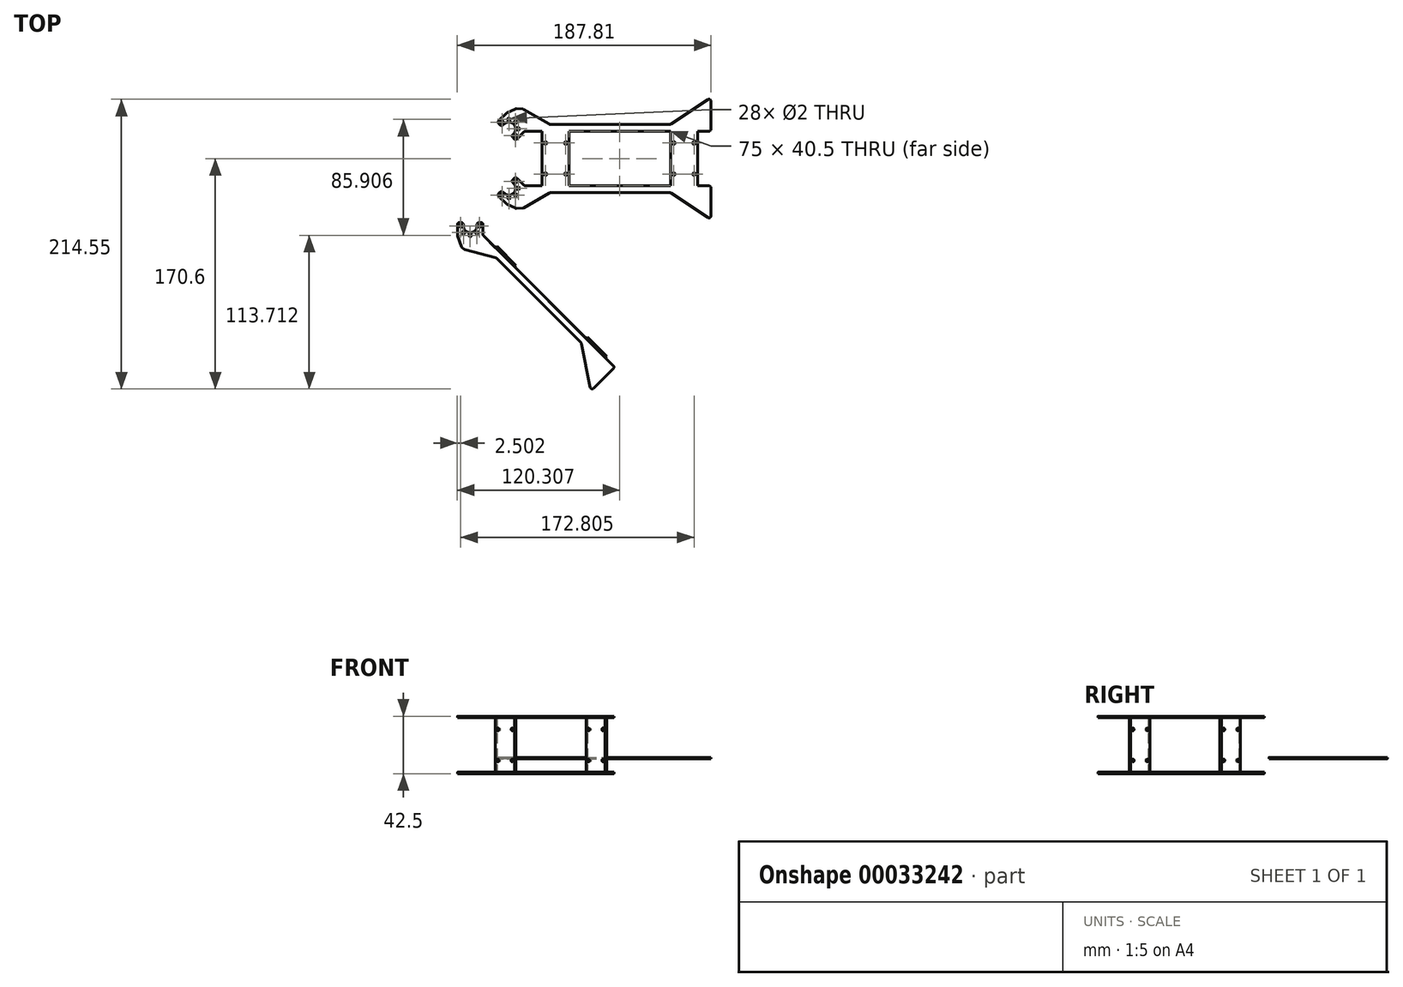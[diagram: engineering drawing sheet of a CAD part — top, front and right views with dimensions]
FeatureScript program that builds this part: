
annotation { "Feature Type Name" : "Feature", "Feature Type Description" : "" }
export const myFeature = defineFeature(function(context is Context, id is Id, definition is map)
    precondition{}
    {
        {
            var Q0;
            Q0=qCreatedBy(makeId("Top.planeOp"),FACE);
            var sketch = newSketch(context, id + "F0", { "sketchPlane" : qUnion([Q0])});
            skArc(sketch, "E0", {"start": v(-5.05, 0) * mm, "mid": v(0, -5.05) * mm, "end": v(5.05, 0) * mm});
            skCircle(sketch, "E1", {"center": v(-7, 0) * mm, "radius": 1 * mm});
            skCircle(sketch, "E2.1.0", {"center": v(-4.95, -4.95) * mm, "radius": 1 * mm});
            skCircle(sketch, "E2.2.0", {"center": v(0, -7) * mm, "radius": 1 * mm});
            skCircle(sketch, "E2.3.0", {"center": v(4.95, -4.95) * mm, "radius": 1 * mm});
            skCircle(sketch, "E2.4.0", {"center": v(7, 0) * mm, "radius": 1 * mm});
            skLineSegment(sketch, "E3", {"start": v(0, 0) * mm, "end": v(106.07, -106.07) * mm, "construction": true});
            skLineSegment(sketch, "E4", {"start": v(9.5, 0) * mm, "end": v(9.5, -7) * mm});
            skLineSegment(sketch, "E5", {"start": v(9.5, -7) * mm, "end": v(107.08, -104.58) * mm});
            skLineSegment(sketch, "E6.MirrorCS", {"start": v(-9.5, 0) * mm, "end": v(-9.5, -7) * mm});
            skLineSegment(sketch, "E7", {"start": v(-9.5, -7) * mm, "end": v(-5.85, -17.02) * mm});
            skLineSegment(sketch, "E8", {"start": v(-5.85, -17.02) * mm, "end": v(19.15, -23.72) * mm});
            skLineSegment(sketch, "E9", {"start": v(19.15, -23.72) * mm, "end": v(103.55, -108.12) * mm});
            skLineSegment(sketch, "E10", {"start": v(107.08, -104.58) * mm, "end": v(103.55, -108.12) * mm});
            skLineSegment(sketch, "E11", {"start": v(-9.5, 0) * mm, "end": v(-9.5, 2.5) * mm});
            skLineSegment(sketch, "E12", {"start": v(-9.5, 2.5) * mm, "end": v(-5.05, 2.5) * mm});
            skLineSegment(sketch, "E13", {"start": v(9.5, 2.5) * mm, "end": v(9.5, 0) * mm});
            skLineSegment(sketch, "E14", {"start": v(-5.05, 0) * mm, "end": v(-5.05, 2.5) * mm});
            skLineSegment(sketch, "E15.MirrorCS", {"start": v(5.05, 0) * mm, "end": v(5.05, 2.5) * mm});
            skLineSegment(sketch, "E16.trimOffspring", {"start": v(5.05, 2.5) * mm, "end": v(9.5, 2.5) * mm});
            skLineSegment(sketch, "E17", {"start": v(103.55, -108.12) * mm, "end": v(89.4, -122.26) * mm});
            skLineSegment(sketch, "E18", {"start": v(89.4, -122.26) * mm, "end": v(82.33, -86.9) * mm});
            skSolve(sketch);
        }
        {
            var Q0;
            Q0=qSketchRegion(id+"F0",true);
            extrude(context, id + "F1", {"entities" : qUnion([Q0]), "depth" : 1 * mm});
        }
        {
            var Q0;
            Q0=makeQuery(id+"F1.opExtrude","SWEPT_EDGE",EDGE,{"disambiguationData":[OSD([sQuery(id+"F0.wireOp",EDGE,"E17"),sQuery(id+"F0.wireOp",EDGE,"E18")])]});
            var Q1;
            Q1=makeQuery(id+"F1.opExtrude","SWEPT_EDGE",EDGE,{"disambiguationData":[OSD([sQuery(id+"F0.wireOp",EDGE,"E9"),sQuery(id+"F0.wireOp",EDGE,"E18")])]});
            var Q2;
            Q2=makeQuery(id+"F1.opExtrude","SWEPT_EDGE",EDGE,{"disambiguationData":[OSD([sQuery(id+"F0.wireOp",EDGE,"E5"),sQuery(id+"F0.wireOp",EDGE,"E10")])]});
            var Q3;
            Q3=makeQuery(id+"F1.opExtrude","SWEPT_EDGE",EDGE,{"disambiguationData":[OSD([sQuery(id+"F0.wireOp",EDGE,"E8"),sQuery(id+"F0.wireOp",EDGE,"E9")])]});
            var Q4;
            Q4=makeQuery(id+"F1.opExtrude","SWEPT_EDGE",EDGE,{"disambiguationData":[OSD([sQuery(id+"F0.wireOp",EDGE,"E4"),sQuery(id+"F0.wireOp",EDGE,"E5")])]});
            var Q5;
            Q5=makeQuery(id+"F1.opExtrude","SWEPT_EDGE",EDGE,{"disambiguationData":[OSD([sQuery(id+"F0.wireOp",EDGE,"E13"),sQuery(id+"F0.wireOp",EDGE,"E16.trimOffspring")])]});
            var Q6;
            Q6=makeQuery(id+"F1.opExtrude","SWEPT_EDGE",EDGE,{"disambiguationData":[OSD([sQuery(id+"F0.wireOp",EDGE,"E12"),sQuery(id+"F0.wireOp",EDGE,"E14")])]});
            var Q7;
            Q7=makeQuery(id+"F1.opExtrude","SWEPT_EDGE",EDGE,{"disambiguationData":[OSD([sQuery(id+"F0.wireOp",EDGE,"E15.MirrorCS"),sQuery(id+"F0.wireOp",EDGE,"E16.trimOffspring")])]});
            var Q8;
            Q8=makeQuery(id+"F1.opExtrude","SWEPT_EDGE",EDGE,{"disambiguationData":[OSD([sQuery(id+"F0.wireOp",EDGE,"E11"),sQuery(id+"F0.wireOp",EDGE,"E12")])]});
            var Q9;
            Q9=makeQuery(id+"F1.opExtrude","SWEPT_EDGE",EDGE,{"disambiguationData":[OSD([sQuery(id+"F0.wireOp",EDGE,"E6.MirrorCS"),sQuery(id+"F0.wireOp",EDGE,"E7")])]});
            fillet(context, id + "F2", {"entities" : qUnion([Q0, Q1, Q2, Q3, Q4, Q5, Q6, Q7, Q8, Q9]), "radius" : 1.5 * mm, "tangentPropagation" : true, "allowEdgeOverflow" : false});
        }
        {
            var Q0;
            Q0=makeQuery(id+"F1.opExtrude","SWEPT_EDGE",EDGE,{"disambiguationData":[OSD([sQuery(id+"F0.wireOp",EDGE,"E7"),sQuery(id+"F0.wireOp",EDGE,"E8")])]});
            chamfer(context, id + "F3", {"entities" : qUnion([Q0]), "width" : 3 * mm, "tangentPropagation" : true});
        }
        {
            var Q0;
            {var subQ0=sQuery(id+"F0.wireOp",EDGE,"E7");Q0=makeQuery(id+"F3.opChamfer","BLEND_EDGE",EDGE,{"blendedFrom":[makeQuery(id+"F1.opExtrude","SWEPT_EDGE",EDGE,{"disambiguationData":[OSD([subQ0,sQuery(id+"F0.wireOp",EDGE,"E8")])]}),makeQuery(id+"F1.opExtrude","SWEPT_FACE",FACE,{"disambiguationData":[OSD([subQ0])]})],"blendedInto":[makeQuery(id+"F1.opExtrude","SWEPT_FACE",FACE,{"disambiguationData":[OSD([subQ0])]})]});}
            var Q1;
            {var subQ0=sQuery(id+"F0.wireOp",EDGE,"E8");Q1=makeQuery(id+"F3.opChamfer","BLEND_EDGE",EDGE,{"blendedFrom":[makeQuery(id+"F1.opExtrude","SWEPT_EDGE",EDGE,{"disambiguationData":[OSD([sQuery(id+"F0.wireOp",EDGE,"E7"),subQ0])]}),makeQuery(id+"F1.opExtrude","SWEPT_FACE",FACE,{"disambiguationData":[OSD([subQ0])]})],"blendedInto":[makeQuery(id+"F1.opExtrude","SWEPT_FACE",FACE,{"disambiguationData":[OSD([subQ0])]})]});}
            fillet(context, id + "F4", {"entities" : qUnion([Q0, Q1]), "radius" : 1.5 * mm, "tangentPropagation" : true, "allowEdgeOverflow" : false});
        }
        {
            var Q0;
            Q0=makeQuery(id+"F1.opExtrude","CAP_FACE",FACE,{"disambiguationData":[OSD([sQuery(id+"F0.wireOp",EDGE,"E0"),sQuery(id+"F0.wireOp",EDGE,"E1"),sQuery(id+"F0.wireOp",EDGE,"E2.1.0"),sQuery(id+"F0.wireOp",EDGE,"E2.2.0"),sQuery(id+"F0.wireOp",EDGE,"E2.3.0"),sQuery(id+"F0.wireOp",EDGE,"E2.4.0"),sQuery(id+"F0.wireOp",EDGE,"E4"),sQuery(id+"F0.wireOp",EDGE,"E5"),sQuery(id+"F0.wireOp",EDGE,"E6.MirrorCS"),sQuery(id+"F0.wireOp",EDGE,"E7"),sQuery(id+"F0.wireOp",EDGE,"E8"),sQuery(id+"F0.wireOp",EDGE,"E9"),sQuery(id+"F0.wireOp",EDGE,"E10"),sQuery(id+"F0.wireOp",EDGE,"E11"),sQuery(id+"F0.wireOp",EDGE,"E12"),sQuery(id+"F0.wireOp",EDGE,"E13"),sQuery(id+"F0.wireOp",EDGE,"E14"),sQuery(id+"F0.wireOp",EDGE,"E15.MirrorCS"),sQuery(id+"F0.wireOp",EDGE,"E16.trimOffspring"),sQuery(id+"F0.wireOp",EDGE,"E17"),sQuery(id+"F0.wireOp",EDGE,"E18")])],"isStart":false});
            var sketch = newSketch(context, id + "F5", { "sketchPlane" : qUnion([Q0])});
            skLineSegment(sketch, "E19", {"start": v(18.7, -16.2) * mm, "end": v(19.75, -15.13) * mm});
            skLineSegment(sketch, "E20", {"start": v(19.75, -15.13) * mm, "end": v(33.9, -29.27) * mm});
            skLineSegment(sketch, "E21", {"start": v(33.9, -29.27) * mm, "end": v(32.83, -30.33) * mm});
            skLineSegment(sketch, "E22", {"start": v(18.7, -16.2) * mm, "end": v(32.83, -30.33) * mm});
            skLineSegment(sketch, "E23", {"start": v(100, -97.5) * mm, "end": v(85.87, -83.37) * mm});
            skLineSegment(sketch, "E24", {"start": v(85.87, -83.37) * mm, "end": v(86.93, -82.3) * mm});
            skLineSegment(sketch, "E25", {"start": v(86.93, -82.3) * mm, "end": v(101.07, -96.45) * mm});
            skLineSegment(sketch, "E26", {"start": v(101.07, -96.45) * mm, "end": v(100, -97.5) * mm});
            skSolve(sketch);
        }
        {
            var Q0;
            Q0=qSketchRegion(id+"F5",true);
            extrude(context, id + "F6", {"entities" : qUnion([Q0]), "operationType" : NewBodyOperationType.ADD, "depth" : (40.5 / 2) * mm, "hasSecondDirection" : true, "secondDirectionOppositeDirection" : true, "secondDirectionDepth" : 1 * mm});
        }
        {
            var Q0;
            Q0=makeQuery(id+"F6.opExtrude","CAP_FACE",FACE,{"disambiguationData":[OSD([sQuery(id+"F5.wireOp",EDGE,"E19"),sQuery(id+"F5.wireOp",EDGE,"E20"),sQuery(id+"F5.wireOp",EDGE,"E21"),sQuery(id+"F5.wireOp",EDGE,"E22")])],"isStart":false});
            cPlane(context, id + "F7", {"entities" : qUnion([Q0]), "cplaneType" : CPlaneType.OFFSET, "offset" : 0 * mm, "width" : 150 * mm, "height" : 150 * mm});
        }
        {
            var Q0;
            Q0=makeQuery(id+"F1.opExtrude","SWEPT_BODY",BODY,{"disambiguationData":[OSD([sQuery(id+"F0.wireOp",EDGE,"E0"),sQuery(id+"F0.wireOp",EDGE,"E1"),sQuery(id+"F0.wireOp",EDGE,"E2.1.0"),sQuery(id+"F0.wireOp",EDGE,"E2.2.0"),sQuery(id+"F0.wireOp",EDGE,"E2.3.0"),sQuery(id+"F0.wireOp",EDGE,"E2.4.0"),sQuery(id+"F0.wireOp",EDGE,"E4"),sQuery(id+"F0.wireOp",EDGE,"E5"),sQuery(id+"F0.wireOp",EDGE,"E6.MirrorCS"),sQuery(id+"F0.wireOp",EDGE,"E7"),sQuery(id+"F0.wireOp",EDGE,"E8"),sQuery(id+"F0.wireOp",EDGE,"E9"),sQuery(id+"F0.wireOp",EDGE,"E10"),sQuery(id+"F0.wireOp",EDGE,"E11"),sQuery(id+"F0.wireOp",EDGE,"E12"),sQuery(id+"F0.wireOp",EDGE,"E13"),sQuery(id+"F0.wireOp",EDGE,"E14"),sQuery(id+"F0.wireOp",EDGE,"E15.MirrorCS"),sQuery(id+"F0.wireOp",EDGE,"E16.trimOffspring"),sQuery(id+"F0.wireOp",EDGE,"E17"),sQuery(id+"F0.wireOp",EDGE,"E18")])]});
            var Q1;
            Q1=qCreatedBy(id+"F7.planeOp",FACE);
            mirror(context, id + "F8", {"operationType" : NewBodyOperationType.ADD, "entities" : qUnion([Q0]), "mirrorPlane" : qUnion([Q1])});
        }
        {
            var Q0;
            {var subQ0=makeQuery(id+"F6.opExtrude","SWEPT_FACE",FACE,{"disambiguationData":[OSD([sQuery(id+"F5.wireOp",EDGE,"E20")])]});Q0=makeQuery(id+"F8.boolean.opBoolean","MERGE",FACE,{"derivedFrom":[subQ0,makeQuery(id+"F8.opPattern","COPY",FACE,{"derivedFrom":subQ0,"instanceName":"1"})]});}
            var sketch = newSketch(context, id + "F9", { "sketchPlane" : qUnion([Q0])});
            skLineSegment(sketch, "E27", {"start": v(-24.67, 21.25) * mm, "end": v(-44.67, 21.25) * mm, "construction": true});
            skLineSegment(sketch, "E28.bottom", {"start": v(-27.17, 32.75) * mm, "end": v(-42.17, 32.75) * mm, "construction": true});
            skLineSegment(sketch, "E28.top", {"start": v(-27.17, 9.75) * mm, "end": v(-42.17, 9.75) * mm, "construction": true});
            skLineSegment(sketch, "E28.left", {"start": v(-27.17, 32.75) * mm, "end": v(-27.17, 9.75) * mm, "construction": true});
            skLineSegment(sketch, "E28.right", {"start": v(-42.17, 32.75) * mm, "end": v(-42.17, 9.75) * mm, "construction": true});
            skPoint(sketch, "E28.middle", {"position": v(-34.67, 21.25) * mm});
            skCircle(sketch, "E29", {"center": v(-27.17, 32.75) * mm, "radius": 1 * mm});
            skLineSegment(sketch, "E30", {"start": v(-34.67, 32.75) * mm, "end": v(-34.67, 9.75) * mm, "construction": true});
            skCircle(sketch, "E31.MirrorC", {"center": v(-27.17, 9.75) * mm, "radius": 1 * mm});
            skCircle(sketch, "E32.MirrorC", {"center": v(-42.17, 32.75) * mm, "radius": 1 * mm});
            skCircle(sketch, "E33.MirrorC", {"center": v(-42.17, 9.75) * mm, "radius": 1 * mm});
            skLineSegment(sketch, "E34.1.0.0", {"start": v(-122.17, 32.75) * mm, "end": v(-137.17, 32.75) * mm, "construction": true});
            skLineSegment(sketch, "E34.1.0.1", {"start": v(-129.67, 32.75) * mm, "end": v(-129.67, 9.75) * mm, "construction": true});
            skLineSegment(sketch, "E34.1.0.2", {"start": v(-122.17, 32.75) * mm, "end": v(-122.17, 9.75) * mm, "construction": true});
            skLineSegment(sketch, "E34.1.0.3", {"start": v(-119.67, 21.25) * mm, "end": v(-139.67, 21.25) * mm, "construction": true});
            skLineSegment(sketch, "E34.1.0.4", {"start": v(-137.17, 32.75) * mm, "end": v(-137.17, 9.75) * mm, "construction": true});
            skLineSegment(sketch, "E34.1.0.5", {"start": v(-122.17, 9.75) * mm, "end": v(-137.17, 9.75) * mm, "construction": true});
            skPoint(sketch, "E34.1.0.6", {"position": v(-129.67, 21.25) * mm});
            skCircle(sketch, "E34.1.0.7", {"center": v(-137.17, 32.75) * mm, "radius": 1 * mm});
            skCircle(sketch, "E34.1.0.8", {"center": v(-137.17, 9.75) * mm, "radius": 1 * mm});
            skCircle(sketch, "E34.1.0.9", {"center": v(-122.17, 9.75) * mm, "radius": 1 * mm});
            skCircle(sketch, "E34.1.0.10", {"center": v(-122.17, 32.75) * mm, "radius": 1 * mm});
            skLineSegment(sketch, "E34.direction1", {"start": v(-42.17, 9.75) * mm, "end": v(-137.17, 9.75) * mm, "construction": true});
            skSolve(sketch);
        }
        {
            var Q0;
            Q0=qSketchRegion(id+"F9",true);
            extrude(context, id + "F10", {"entities" : qUnion([Q0]), "operationType" : NewBodyOperationType.REMOVE, "endBound" : BoundingType.UP_TO_NEXT, "oppositeDirection" : true, "depth" : 25 * mm});
        }
        {
            var Q0;
            {var subQ0=makeQuery(id+"F6.opExtrude","SWEPT_FACE",FACE,{"disambiguationData":[OSD([sQuery(id+"F5.wireOp",EDGE,"E26")])]});Q0=makeQuery(id+"F8.boolean.opBoolean","MERGE",FACE,{"derivedFrom":[subQ0,makeQuery(id+"F8.opPattern","COPY",FACE,{"derivedFrom":subQ0,"instanceName":"1"})]});}
            var sketch = newSketch(context, id + "F11", { "sketchPlane" : qUnion([Q0])});
            skLineSegment(sketch, "E35.bottom", {"start": v(1.77, 42.5) * mm, "end": v(3.27, 42.5) * mm});
            skLineSegment(sketch, "E35.top", {"start": v(1.77, 41.5) * mm, "end": v(3.27, 41.5) * mm});
            skLineSegment(sketch, "E35.left", {"start": v(1.77, 42.5) * mm, "end": v(1.77, 41.5) * mm});
            skLineSegment(sketch, "E35.right", {"start": v(3.27, 42.5) * mm, "end": v(3.27, 41.5) * mm});
            skLineSegment(sketch, "E36.bottom", {"start": v(1.77, 0) * mm, "end": v(3.27, 0) * mm});
            skLineSegment(sketch, "E36.top", {"start": v(1.77, 1) * mm, "end": v(3.27, 1) * mm});
            skLineSegment(sketch, "E36.left", {"start": v(1.77, 0) * mm, "end": v(1.77, 1) * mm});
            skLineSegment(sketch, "E36.right", {"start": v(3.27, 0) * mm, "end": v(3.27, 1) * mm});
            skSolve(sketch);
        }
        {
            var Q0;
            Q0 = qSketchRegion(id + "F11", true);
            var Q1;
            {var subQ0=makeQuery(id+"F6.opExtrude","SWEPT_FACE",FACE,{"disambiguationData":[OSD([sQuery(id+"F5.wireOp",EDGE,"E19")])]});Q1=makeQuery(id+"F8.boolean.opBoolean","MERGE",FACE,{"derivedFrom":[subQ0,makeQuery(id+"F8.opPattern","COPY",FACE,{"derivedFrom":subQ0,"instanceName":"1"})]});}
            extrude(context, id + "F12", {"entities" : qUnion([Q0]), "operationType" : NewBodyOperationType.REMOVE, "endBound" : BoundingType.UP_TO_SURFACE, "oppositeDirection" : true, "endBoundEntityFace" : qUnion([Q1]), "depth" : 25 * mm});
        }
        {
            var Q0;
            Q0=makeQuery(id+"F12.boolean.opBoolean","SPLIT",BODY,{"disambiguationData":[OD(0.0)],"derivedFrom":makeQuery(id+"F1.opExtrude","SWEPT_BODY",BODY,{"disambiguationData":[OSD([sQuery(id+"F0.wireOp",EDGE,"E0"),sQuery(id+"F0.wireOp",EDGE,"E1"),sQuery(id+"F0.wireOp",EDGE,"E2.1.0"),sQuery(id+"F0.wireOp",EDGE,"E2.2.0"),sQuery(id+"F0.wireOp",EDGE,"E2.3.0"),sQuery(id+"F0.wireOp",EDGE,"E2.4.0"),sQuery(id+"F0.wireOp",EDGE,"E4"),sQuery(id+"F0.wireOp",EDGE,"E5"),sQuery(id+"F0.wireOp",EDGE,"E6.MirrorCS"),sQuery(id+"F0.wireOp",EDGE,"E7"),sQuery(id+"F0.wireOp",EDGE,"E8"),sQuery(id+"F0.wireOp",EDGE,"E9"),sQuery(id+"F0.wireOp",EDGE,"E10"),sQuery(id+"F0.wireOp",EDGE,"E11"),sQuery(id+"F0.wireOp",EDGE,"E12"),sQuery(id+"F0.wireOp",EDGE,"E13"),sQuery(id+"F0.wireOp",EDGE,"E14"),sQuery(id+"F0.wireOp",EDGE,"E15.MirrorCS"),sQuery(id+"F0.wireOp",EDGE,"E16.trimOffspring"),sQuery(id+"F0.wireOp",EDGE,"E17"),sQuery(id+"F0.wireOp",EDGE,"E18")])]})});
            var Q1;
            {var subQ0=sQuery(id+"F5.wireOp",EDGE,"E26");var subQ1=sQuery(id+"F5.wireOp",EDGE,"E23");var subQ2=sQuery(id+"F0.wireOp",EDGE,"E5");var subQ3=makeQuery(id+"F6.opExtrude","SWEPT_FACE",FACE,{"disambiguationData":[OSD([sQuery(id+"F5.wireOp",EDGE,"E22")])]});var subQ4=makeQuery(id+"F6.opExtrude","SWEPT_FACE",FACE,{"disambiguationData":[OSD([sQuery(id+"F5.wireOp",EDGE,"E21")])]});var subQ5=makeQuery(id+"F1.opExtrude","SWEPT_FACE",FACE,{"disambiguationData":[OSD([subQ2])]});var subQ6=sQuery(id+"F0.wireOp",EDGE,"E10");var subQ7=sQuery(id+"F0.wireOp",EDGE,"E4");var subQ8=makeQuery(id+"F1.opExtrude","CAP_FACE",FACE,{"disambiguationData":[OSD([sQuery(id+"F0.wireOp",EDGE,"E0"),sQuery(id+"F0.wireOp",EDGE,"E1"),sQuery(id+"F0.wireOp",EDGE,"E2.1.0"),sQuery(id+"F0.wireOp",EDGE,"E2.2.0"),sQuery(id+"F0.wireOp",EDGE,"E2.3.0"),sQuery(id+"F0.wireOp",EDGE,"E2.4.0"),subQ7,subQ2,sQuery(id+"F0.wireOp",EDGE,"E6.MirrorCS"),sQuery(id+"F0.wireOp",EDGE,"E7"),sQuery(id+"F0.wireOp",EDGE,"E8"),sQuery(id+"F0.wireOp",EDGE,"E9"),subQ6,sQuery(id+"F0.wireOp",EDGE,"E11"),sQuery(id+"F0.wireOp",EDGE,"E12"),sQuery(id+"F0.wireOp",EDGE,"E13"),sQuery(id+"F0.wireOp",EDGE,"E14"),sQuery(id+"F0.wireOp",EDGE,"E15.MirrorCS"),sQuery(id+"F0.wireOp",EDGE,"E16.trimOffspring"),sQuery(id+"F0.wireOp",EDGE,"E17"),sQuery(id+"F0.wireOp",EDGE,"E18")])],"isStart":false});var subQ9=makeQuery(id+"F6.opExtrude","SWEPT_FACE",FACE,{"disambiguationData":[OSD([subQ1])]});var subQ10=makeQuery(id+"F6.opExtrude","SWEPT_FACE",FACE,{"disambiguationData":[OSD([sQuery(id+"F5.wireOp",EDGE,"E24")])]});var subQ11=makeQuery(id+"F1.opExtrude","CAP_EDGE",EDGE,{"disambiguationData":[OSD([subQ2])],"isStart":false});var subQ12=makeQuery(id+"F6.opExtrude","SWEPT_FACE",FACE,{"disambiguationData":[OSD([subQ0])]});var subQ13=makeQuery(id+"F6.opExtrude","SWEPT_FACE",FACE,{"disambiguationData":[OSD([sQuery(id+"F5.wireOp",EDGE,"E19")])]});Q1=makeQuery(id+"F12.boolean.opBoolean","MERGE",EDGE,{"derivedFrom":[makeQuery(id+"F6.boolean.opBoolean","SPLIT",EDGE,{"disambiguationData":[TD([subQ8,subQ5,makeQuery(id+"F2.opFillet","BLEND_FACE",FACE,{"disambiguationData":[OSD([subQ7,subQ2])]}),subQ13,subQ3])],"derivedFrom":subQ11}),makeQuery(id+"F6.boolean.opBoolean","SPLIT",EDGE,{"disambiguationData":[TD([subQ8,subQ5,makeQuery(id+"F2.opFillet","BLEND_FACE",FACE,{"disambiguationData":[OSD([subQ2,subQ6])]}),subQ9,subQ12])],"derivedFrom":subQ11}),makeQuery(id+"F6.boolean.opBoolean","SPLIT",EDGE,{"disambiguationData":[TD([subQ8,subQ5,subQ13,subQ4,subQ3])],"derivedFrom":subQ11}),makeQuery(id+"F6.boolean.opBoolean","SPLIT",EDGE,{"disambiguationData":[TD([subQ8,subQ5,subQ9,subQ10,subQ12])],"derivedFrom":subQ11}),makeQuery(id+"F6.boolean.opBoolean","SPLIT",EDGE,{"disambiguationData":[TD([subQ8,subQ5,subQ4,subQ3,subQ9,subQ10])],"derivedFrom":subQ11}),makeQuery(id+"F12.opExtrude","SWEPT_EDGE",EDGE,{"disambiguationData":[OSD([subQ2,subQ1,subQ0,sQuery(id+"F11.wireOp",EDGE,"E36.top"),sQuery(id+"F11.wireOp",EDGE,"E36.left")])]})]});}
            transform(context, id + "F13", {"entities" : qUnion([Q0]), "transformType" : TransformType.ROTATION, "transformAxis" : qUnion([Q1]), "angle" : 90 * degree, "makeCopy" : false});
        }
        {
            var Q0;
            Q0=makeQuery(id+"F12.boolean.opBoolean","SPLIT",BODY,{"disambiguationData":[OD(1.0)],"derivedFrom":makeQuery(id+"F1.opExtrude","SWEPT_BODY",BODY,{"disambiguationData":[OSD([sQuery(id+"F0.wireOp",EDGE,"E0"),sQuery(id+"F0.wireOp",EDGE,"E1"),sQuery(id+"F0.wireOp",EDGE,"E2.1.0"),sQuery(id+"F0.wireOp",EDGE,"E2.2.0"),sQuery(id+"F0.wireOp",EDGE,"E2.3.0"),sQuery(id+"F0.wireOp",EDGE,"E2.4.0"),sQuery(id+"F0.wireOp",EDGE,"E4"),sQuery(id+"F0.wireOp",EDGE,"E5"),sQuery(id+"F0.wireOp",EDGE,"E6.MirrorCS"),sQuery(id+"F0.wireOp",EDGE,"E7"),sQuery(id+"F0.wireOp",EDGE,"E8"),sQuery(id+"F0.wireOp",EDGE,"E9"),sQuery(id+"F0.wireOp",EDGE,"E10"),sQuery(id+"F0.wireOp",EDGE,"E11"),sQuery(id+"F0.wireOp",EDGE,"E12"),sQuery(id+"F0.wireOp",EDGE,"E13"),sQuery(id+"F0.wireOp",EDGE,"E14"),sQuery(id+"F0.wireOp",EDGE,"E15.MirrorCS"),sQuery(id+"F0.wireOp",EDGE,"E16.trimOffspring"),sQuery(id+"F0.wireOp",EDGE,"E17"),sQuery(id+"F0.wireOp",EDGE,"E18")])]})});
            var Q1;
            {var subQ0=sQuery(id+"F0.wireOp",EDGE,"E5");Q1=makeQuery(id+"F12.boolean.opBoolean","MERGE",EDGE,{"derivedFrom":[makeQuery(id+"F8.opPattern","COPY",EDGE,{"derivedFrom":makeQuery(id+"F6.boolean.opBoolean","SPLIT",EDGE,{"disambiguationData":[TD([makeQuery(id+"F1.opExtrude","CAP_FACE",FACE,{"disambiguationData":[OSD([sQuery(id+"F0.wireOp",EDGE,"E0"),sQuery(id+"F0.wireOp",EDGE,"E1"),sQuery(id+"F0.wireOp",EDGE,"E2.1.0"),sQuery(id+"F0.wireOp",EDGE,"E2.2.0"),sQuery(id+"F0.wireOp",EDGE,"E2.3.0"),sQuery(id+"F0.wireOp",EDGE,"E2.4.0"),sQuery(id+"F0.wireOp",EDGE,"E4"),subQ0,sQuery(id+"F0.wireOp",EDGE,"E6.MirrorCS"),sQuery(id+"F0.wireOp",EDGE,"E7"),sQuery(id+"F0.wireOp",EDGE,"E8"),sQuery(id+"F0.wireOp",EDGE,"E9"),sQuery(id+"F0.wireOp",EDGE,"E10"),sQuery(id+"F0.wireOp",EDGE,"E11"),sQuery(id+"F0.wireOp",EDGE,"E12"),sQuery(id+"F0.wireOp",EDGE,"E13"),sQuery(id+"F0.wireOp",EDGE,"E14"),sQuery(id+"F0.wireOp",EDGE,"E15.MirrorCS"),sQuery(id+"F0.wireOp",EDGE,"E16.trimOffspring"),sQuery(id+"F0.wireOp",EDGE,"E17"),sQuery(id+"F0.wireOp",EDGE,"E18")])],"isStart":false}),makeQuery(id+"F1.opExtrude","SWEPT_FACE",FACE,{"disambiguationData":[OSD([subQ0])]}),makeQuery(id+"F6.opExtrude","SWEPT_FACE",FACE,{"disambiguationData":[OSD([sQuery(id+"F5.wireOp",EDGE,"E19")])]}),makeQuery(id+"F6.opExtrude","SWEPT_FACE",FACE,{"disambiguationData":[OSD([sQuery(id+"F5.wireOp",EDGE,"E21")])]}),makeQuery(id+"F6.opExtrude","SWEPT_FACE",FACE,{"disambiguationData":[OSD([sQuery(id+"F5.wireOp",EDGE,"E22")])]})])],"derivedFrom":makeQuery(id+"F1.opExtrude","CAP_EDGE",EDGE,{"disambiguationData":[OSD([subQ0])],"isStart":false})}),"instanceName":"1"}),makeQuery(id+"F12.opExtrude","SWEPT_EDGE",EDGE,{"disambiguationData":[OSD([subQ0,sQuery(id+"F5.wireOp",EDGE,"E23"),sQuery(id+"F5.wireOp",EDGE,"E26"),sQuery(id+"F11.wireOp",EDGE,"E35.top"),sQuery(id+"F11.wireOp",EDGE,"E35.left")])]})]});}
            transform(context, id + "F14", {"entities" : qUnion([Q0]), "transformType" : TransformType.ROTATION, "transformAxis" : qUnion([Q1]), "angle" : 270 * degree, "makeCopy" : false});
        }
        {
            var Q0;
            Q0=makeQuery(id+"F1.opExtrude","CAP_FACE",FACE,{"disambiguationData":[OSD([sQuery(id+"F0.wireOp",EDGE,"E0"),sQuery(id+"F0.wireOp",EDGE,"E1"),sQuery(id+"F0.wireOp",EDGE,"E2.1.0"),sQuery(id+"F0.wireOp",EDGE,"E2.2.0"),sQuery(id+"F0.wireOp",EDGE,"E2.3.0"),sQuery(id+"F0.wireOp",EDGE,"E2.4.0"),sQuery(id+"F0.wireOp",EDGE,"E4"),sQuery(id+"F0.wireOp",EDGE,"E5"),sQuery(id+"F0.wireOp",EDGE,"E6.MirrorCS"),sQuery(id+"F0.wireOp",EDGE,"E7"),sQuery(id+"F0.wireOp",EDGE,"E8"),sQuery(id+"F0.wireOp",EDGE,"E9"),sQuery(id+"F0.wireOp",EDGE,"E10"),sQuery(id+"F0.wireOp",EDGE,"E11"),sQuery(id+"F0.wireOp",EDGE,"E12"),sQuery(id+"F0.wireOp",EDGE,"E13"),sQuery(id+"F0.wireOp",EDGE,"E14"),sQuery(id+"F0.wireOp",EDGE,"E15.MirrorCS"),sQuery(id+"F0.wireOp",EDGE,"E16.trimOffspring"),sQuery(id+"F0.wireOp",EDGE,"E17"),sQuery(id+"F0.wireOp",EDGE,"E18")])],"isStart":false});
            cPlane(context, id + "F15", {"entities" : qUnion([Q0]), "cplaneType" : CPlaneType.OFFSET, "offset" : 10 * mm, "width" : 150 * mm, "height" : 150 * mm});
        }
        {
            var Q0;
            Q0=qCreatedBy(id+"F15.planeOp",FACE);
            var sketch = newSketch(context, id + "F16", { "sketchPlane" : qUnion([Q0])});
            skLineSegment(sketch, "E37.0", {"start": v(-1.95, -12.25) * mm, "end": v(-7.42, -6.78) * mm});
            skLineSegment(sketch, "E37.1", {"start": v(10.81, -15.26) * mm, "end": v(29.96, -4.2) * mm});
            skLineSegment(sketch, "E37.2", {"start": v(12.29, 1) * mm, "end": v(148.17, 1) * mm});
            skCircle(sketch, "E37.3", {"center": v(4.95, -5.72) * mm, "radius": 1 * mm});
            skArc(sketch, "E37.4", {"start": v(-3.57, 46.84) * mm, "mid": v(3.57, 46.84) * mm, "end": v(3.57, 39.7) * mm});
            skCircle(sketch, "E37.5", {"center": v(4.95, 48.22) * mm, "radius": 1 * mm});
            skLineSegment(sketch, "E37.6", {"start": v(-1.95, 54.75) * mm, "end": v(-7.42, 49.28) * mm});
            skLineSegment(sketch, "E37.7", {"start": v(147.34, 64.95) * mm, "end": v(120.05, 46.75) * mm});
            skLineSegment(sketch, "E37.8", {"start": v(10.81, 57.76) * mm, "end": v(29.96, 46.7) * mm});
            skLineSegment(sketch, "E37.9", {"start": v(6.01, 35.84) * mm, "end": v(11.23, 41.06) * mm});
            skLineSegment(sketch, "E37.10", {"start": v(12.29, 41.5) * mm, "end": v(148.17, 41.5) * mm});
            skCircle(sketch, "E37.11", {"center": v(122.17, 9.75) * mm, "radius": 1 * mm});
            skCircle(sketch, "E37.12", {"center": v(137.17, 32.75) * mm, "radius": 1 * mm});
            skCircle(sketch, "E37.13", {"center": v(122.17, 32.75) * mm, "radius": 1 * mm});
            skLineSegment(sketch, "E37.14", {"start": v(24.67, 41.5) * mm, "end": v(44.67, 41.5) * mm});
            skCircle(sketch, "E37.15", {"center": v(42.17, 9.75) * mm, "radius": 1 * mm});
            skLineSegment(sketch, "E37.16", {"start": v(24.67, 41.5) * mm, "end": v(24.67, 1) * mm});
            skCircle(sketch, "E37.17", {"center": v(42.17, 32.75) * mm, "radius": 1 * mm});
            skLineSegment(sketch, "E38.0", {"start": v(147.34, -22.45) * mm, "end": v(120.05, -4.25) * mm});
            skCircle(sketch, "E38.1", {"center": v(0, -7.77) * mm, "radius": 1 * mm});
            skLineSegment(sketch, "E38.2", {"start": v(-1.53, -12.55) * mm, "end": v(4.84, -15.52) * mm});
            skLineSegment(sketch, "E38.3", {"start": v(6.01, 6.66) * mm, "end": v(11.23, 1.44) * mm});
            skArc(sketch, "E38.5", {"start": v(-3.57, -4.34) * mm, "mid": v(3.57, -4.34) * mm, "end": v(3.57, 2.8) * mm});
            skLineSegment(sketch, "E39.0", {"start": v(149.67, -0.5) * mm, "end": v(149.67, -21.2) * mm});
            skPoint(sketch, "E40.0", {"position": v(149.23, 0.56) * mm});
            skArc(sketch, "E41.0", {"start": v(149.67, -0.5) * mm, "mid": v(149.23, 0.56) * mm, "end": v(148.17, 1) * mm});
            skArc(sketch, "E42.0", {"start": v(147.34, -22.45) * mm, "mid": v(148.88, -22.52) * mm, "end": v(149.67, -21.2) * mm});
            skCircle(sketch, "E43.0", {"center": v(137.17, 9.75) * mm, "radius": 1 * mm});
            skLineSegment(sketch, "E44.0", {"start": v(139.67, 41.5) * mm, "end": v(139.67, 1) * mm});
            skLineSegment(sketch, "E45.0", {"start": v(30.71, -4) * mm, "end": v(119.21, -4) * mm});
            skArc(sketch, "E46.0", {"start": v(119.21, -4) * mm, "mid": v(119.65, -4.06) * mm, "end": v(120.05, -4.25) * mm});
            skLineSegment(sketch, "E47.0", {"start": v(149.67, 43) * mm, "end": v(149.67, 63.7) * mm});
            skArc(sketch, "E48.0", {"start": v(147.34, 64.95) * mm, "mid": v(148.88, 65.02) * mm, "end": v(149.67, 63.7) * mm});
            skArc(sketch, "E49.0", {"start": v(149.67, 43) * mm, "mid": v(149.23, 41.94) * mm, "end": v(148.17, 41.5) * mm});
            skLineSegment(sketch, "E50.0", {"start": v(119.67, 41.5) * mm, "end": v(119.67, 1) * mm});
            skLineSegment(sketch, "E51.0", {"start": v(30.71, 46.5) * mm, "end": v(119.21, 46.5) * mm});
            skArc(sketch, "E52.0", {"start": v(119.21, 46.5) * mm, "mid": v(119.65, 46.56) * mm, "end": v(120.05, 46.75) * mm});
            skCircle(sketch, "E53.0", {"center": v(27.17, 9.75) * mm, "radius": 1 * mm});
            skCircle(sketch, "E54.0", {"center": v(27.17, 32.75) * mm, "radius": 1 * mm});
            skArc(sketch, "E55.0", {"start": v(29.96, 46.7) * mm, "mid": v(30.32, 46.55) * mm, "end": v(30.71, 46.5) * mm});
            skArc(sketch, "E56.0", {"start": v(29.96, -4.2) * mm, "mid": v(30.32, -4.05) * mm, "end": v(30.71, -4) * mm});
            skCircle(sketch, "E57.0", {"center": v(7, 43.27) * mm, "radius": 1 * mm});
            skCircle(sketch, "E58.0", {"center": v(0, 50.27) * mm, "radius": 1 * mm});
            skCircle(sketch, "E59.0", {"center": v(-4.95, 48.22) * mm, "radius": 1 * mm});
            skCircle(sketch, "E60.0", {"center": v(4.95, 38.32) * mm, "radius": 1 * mm});
            skCircle(sketch, "E61.0", {"center": v(4.95, 4.18) * mm, "radius": 1 * mm});
            skCircle(sketch, "E62.0", {"center": v(-4.95, -5.72) * mm, "radius": 1 * mm});
            skCircle(sketch, "E63.0", {"center": v(7, -0.77) * mm, "radius": 1 * mm});
            skLineSegment(sketch, "E64.0", {"start": v(5.54, -15.66) * mm, "end": v(10.13, -15.46) * mm});
            skArc(sketch, "E65.0", {"start": v(10.13, -15.46) * mm, "mid": v(10.48, -15.4) * mm, "end": v(10.81, -15.26) * mm});
            skArc(sketch, "E66.0", {"start": v(4.84, -15.52) * mm, "mid": v(5.18, -15.63) * mm, "end": v(5.54, -15.66) * mm});
            skArc(sketch, "E67.0", {"start": v(-1.95, -12.25) * mm, "mid": v(-1.75, -12.42) * mm, "end": v(-1.53, -12.55) * mm});
            skArc(sketch, "E68.0", {"start": v(12.29, 1) * mm, "mid": v(11.71, 1.11) * mm, "end": v(11.23, 1.44) * mm});
            skLineSegment(sketch, "E69.0", {"start": v(3.57, 2.8) * mm, "end": v(2.86, 3.51) * mm});
            skArc(sketch, "E70.0", {"start": v(2.86, 5.63) * mm, "mid": v(2.42, 4.57) * mm, "end": v(2.86, 3.51) * mm});
            skLineSegment(sketch, "E71.0", {"start": v(2.86, 5.63) * mm, "end": v(3.89, 6.66) * mm});
            skArc(sketch, "E72.0", {"start": v(6.01, 6.66) * mm, "mid": v(4.95, 7.1) * mm, "end": v(3.89, 6.66) * mm});
            skArc(sketch, "E73.0", {"start": v(-7.42, -4.66) * mm, "mid": v(-7.86, -5.72) * mm, "end": v(-7.42, -6.78) * mm});
            skLineSegment(sketch, "E74.0", {"start": v(-7.42, -4.66) * mm, "end": v(-6.4, -3.63) * mm});
            skArc(sketch, "E75.0", {"start": v(-4.28, -3.63) * mm, "mid": v(-5.34, -3.2) * mm, "end": v(-6.4, -3.63) * mm});
            skLineSegment(sketch, "E76.0", {"start": v(-3.57, -4.34) * mm, "end": v(-4.28, -3.63) * mm});
            skArc(sketch, "E77.0", {"start": v(-7.42, 47.16) * mm, "mid": v(-7.86, 48.22) * mm, "end": v(-7.42, 49.28) * mm});
            skLineSegment(sketch, "E78.0", {"start": v(-7.42, 47.16) * mm, "end": v(-6.4, 46.13) * mm});
            skArc(sketch, "E79.0", {"start": v(-4.28, 46.13) * mm, "mid": v(-5.34, 45.7) * mm, "end": v(-6.4, 46.13) * mm});
            skLineSegment(sketch, "E80.0", {"start": v(-3.57, 46.84) * mm, "end": v(-4.28, 46.13) * mm});
            skArc(sketch, "E81.0", {"start": v(6.01, 35.84) * mm, "mid": v(4.95, 35.4) * mm, "end": v(3.89, 35.84) * mm});
            skLineSegment(sketch, "E82.0", {"start": v(2.86, 36.87) * mm, "end": v(3.89, 35.84) * mm});
            skArc(sketch, "E83.0", {"start": v(2.86, 36.87) * mm, "mid": v(2.42, 37.93) * mm, "end": v(2.86, 38.99) * mm});
            skLineSegment(sketch, "E84.0", {"start": v(3.57, 39.7) * mm, "end": v(2.86, 38.99) * mm});
            skLineSegment(sketch, "E85.0", {"start": v(-1.53, 55.05) * mm, "end": v(4.84, 58.02) * mm});
            skLineSegment(sketch, "E86.0", {"start": v(5.54, 58.16) * mm, "end": v(10.13, 57.96) * mm});
            skArc(sketch, "E87.0", {"start": v(4.84, 58.02) * mm, "mid": v(5.18, 58.13) * mm, "end": v(5.54, 58.16) * mm});
            skArc(sketch, "E88.0", {"start": v(10.13, 57.96) * mm, "mid": v(10.48, 57.9) * mm, "end": v(10.81, 57.76) * mm});
            skArc(sketch, "E89.0", {"start": v(12.29, 41.5) * mm, "mid": v(11.71, 41.39) * mm, "end": v(11.23, 41.06) * mm});
            skLineSegment(sketch, "E90.0", {"start": v(44.67, 41.5) * mm, "end": v(44.67, 1) * mm});
            skArc(sketch, "E91.0", {"start": v(-1.95, 54.75) * mm, "mid": v(-1.75, 54.92) * mm, "end": v(-1.53, 55.05) * mm});
            skSolve(sketch);
        }
        {
            var Q0;
            Q0 = qSketchRegion(id + "F16", true);
            extrude(context, id + "F17", {"entities" : qUnion([Q0]), "depth" : 1 * mm});
        }
    });
